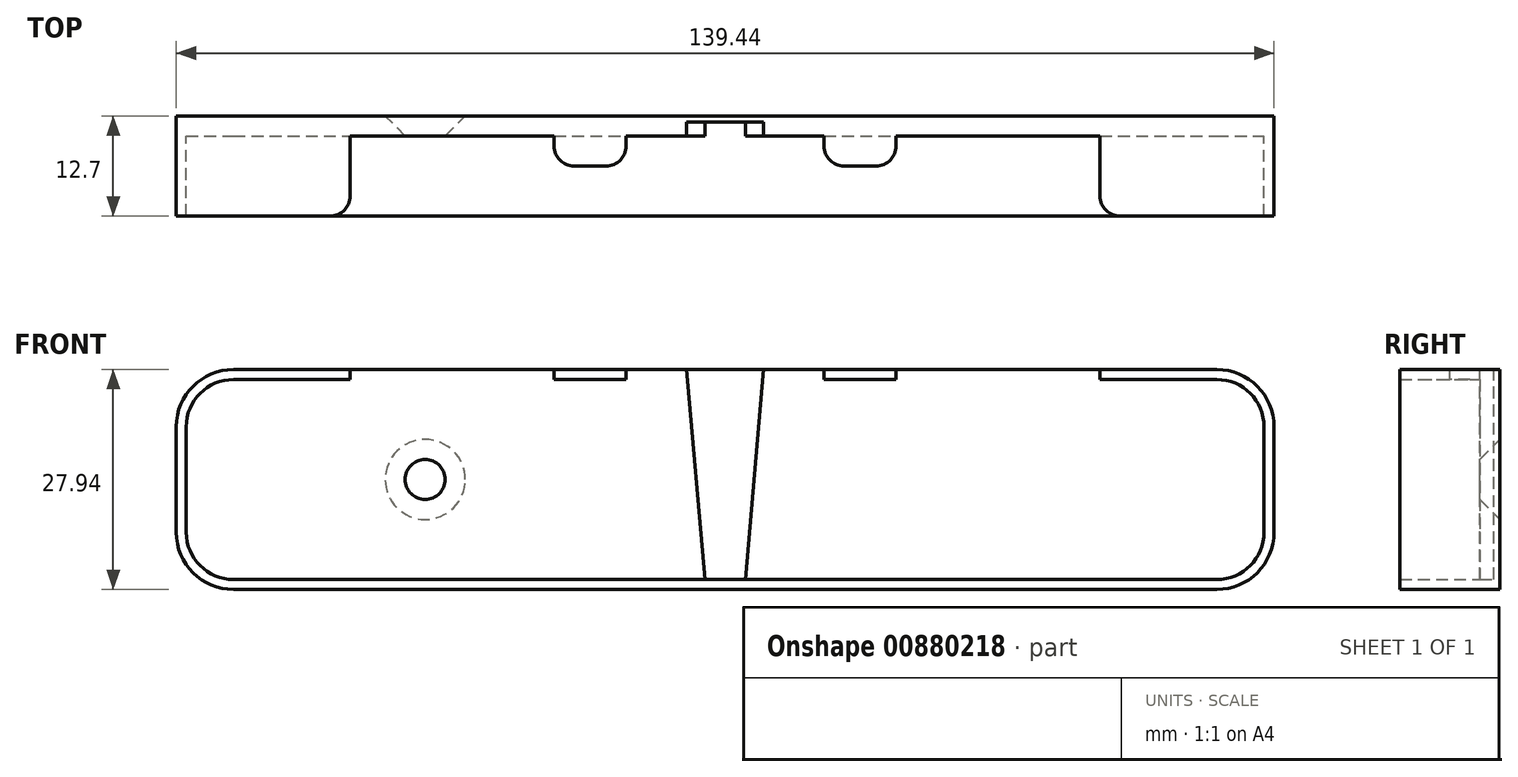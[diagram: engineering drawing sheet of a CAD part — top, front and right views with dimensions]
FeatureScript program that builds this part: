
annotation { "Feature Type Name" : "Feature", "Feature Type Description" : "" }
export const myFeature = defineFeature(function(context is Context, id is Id, definition is map)
    precondition{}
    {
        {
            var Q0;
            Q0=qCreatedBy(makeId("Front.planeOp"),FACE);
            var sketch = newSketch(context, id + "F0", { "sketchPlane" : qUnion([Q0])});
            skLineSegment(sketch, "E0.bottom", {"start": v(-69.72, 13.97) * mm, "end": v(69.72, 13.97) * mm});
            skLineSegment(sketch, "E0.top", {"start": v(-69.72, -13.97) * mm, "end": v(69.72, -13.97) * mm});
            skLineSegment(sketch, "E0.left", {"start": v(-69.72, 13.97) * mm, "end": v(-69.72, -13.97) * mm});
            skLineSegment(sketch, "E0.right", {"start": v(69.72, 13.97) * mm, "end": v(69.72, -13.97) * mm});
            skPoint(sketch, "E0.middle", {"position": v(0, 0) * mm});
            skLineSegment(sketch, "E1.bottom", {"start": v(-68.45, 12.7) * mm, "end": v(68.45, 12.7) * mm});
            skLineSegment(sketch, "E1.top", {"start": v(-68.45, -12.7) * mm, "end": v(68.45, -12.7) * mm});
            skLineSegment(sketch, "E1.left", {"start": v(-68.45, 12.7) * mm, "end": v(-68.45, -12.7) * mm});
            skLineSegment(sketch, "E1.right", {"start": v(68.45, 12.7) * mm, "end": v(68.45, -12.7) * mm});
            skLineSegment(sketch, "E2", {"start": v(47.62, 12.7) * mm, "end": v(47.62, 13.97) * mm});
            skLineSegment(sketch, "E3", {"start": v(21.72, 12.7) * mm, "end": v(21.72, 13.97) * mm});
            skLineSegment(sketch, "E4", {"start": v(12.57, 12.7) * mm, "end": v(12.57, 13.97) * mm});
            skLineSegment(sketch, "E5.MirrorCS", {"start": v(-12.57, 12.7) * mm, "end": v(-12.57, 13.97) * mm});
            skLineSegment(sketch, "E6.MirrorCS", {"start": v(-21.72, 12.7) * mm, "end": v(-21.72, 13.97) * mm});
            skLineSegment(sketch, "E7.MirrorCS", {"start": v(-47.62, 12.7) * mm, "end": v(-47.62, 13.97) * mm});
            skLineSegment(sketch, "E8", {"start": v(2.54, -12.94) * mm, "end": v(4.9, 13.97) * mm});
            skLineSegment(sketch, "E9.MirrorCS", {"start": v(-2.54, -12.94) * mm, "end": v(-4.9, 13.97) * mm});
            skSolve(sketch);
        }
        {
            var Q0;
            Q0=makeQuery(id+"F0.imprint","IMPRINT",FACE,{"disambiguationData":[TD([[makeQuery(id+"F0.imprint","IMPRINT",EDGE,{"derivedFrom":sQuery(id+"F0.wireOp",EDGE,"E0.bottom")}),-1.0]])]});
            extrude(context, id + "F1", {"entities" : qUnion([Q0]), "depth" : 12.7 * mm, "offsetDistance" : 25.4 * mm});
        }
        {
            var Q0;
            Q0=makeQuery(id+"F0.imprint","IMPRINT",FACE,{"disambiguationData":[TD([[makeQuery(id+"F0.imprint","IMPRINT",EDGE,{"derivedFrom":sQuery(id+"F0.wireOp",EDGE,"E1.bottom")}),-1.0]])]});
            extrude(context, id + "F2", {"entities" : qUnion([Q0]), "operationType" : NewBodyOperationType.ADD, "depth" : 2.54 * mm, "offsetDistance" : 25.4 * mm});
        }
        {
            var Q0;
            Q0=makeQuery(id+"F1.opExtrude","SWEPT_EDGE",EDGE,{"disambiguationData":[OSD([sQuery(id+"F0.wireOp",EDGE,"E1.bottom"),sQuery(id+"F0.wireOp",EDGE,"E1.left")])]});
            var Q1;
            Q1=makeQuery(id+"F1.opExtrude","SWEPT_EDGE",EDGE,{"disambiguationData":[OSD([sQuery(id+"F0.wireOp",EDGE,"E1.top"),sQuery(id+"F0.wireOp",EDGE,"E1.left")])]});
            var Q2;
            Q2=makeQuery(id+"F1.opExtrude","SWEPT_EDGE",EDGE,{"disambiguationData":[OSD([sQuery(id+"F0.wireOp",EDGE,"E1.bottom"),sQuery(id+"F0.wireOp",EDGE,"E1.right")])]});
            var Q3;
            Q3=makeQuery(id+"F1.opExtrude","SWEPT_EDGE",EDGE,{"disambiguationData":[OSD([sQuery(id+"F0.wireOp",EDGE,"E1.top"),sQuery(id+"F0.wireOp",EDGE,"E1.right")])]});
            fillet(context, id + "F3", {"entities" : qUnion([Q0, Q1, Q2, Q3]), "radius" : 6 * mm, "tangentPropagation" : true, "allowEdgeOverflow" : false});
        }
        {
            var Q0;
            Q0=makeQuery(id+"F1.opExtrude","SWEPT_EDGE",EDGE,{"disambiguationData":[OSD([sQuery(id+"F0.wireOp",EDGE,"E0.bottom"),sQuery(id+"F0.wireOp",EDGE,"E0.left")])]});
            var Q1;
            Q1=makeQuery(id+"F1.opExtrude","SWEPT_EDGE",EDGE,{"disambiguationData":[OSD([sQuery(id+"F0.wireOp",EDGE,"E0.top"),sQuery(id+"F0.wireOp",EDGE,"E0.left")])]});
            var Q2;
            Q2=makeQuery(id+"F1.opExtrude","SWEPT_EDGE",EDGE,{"disambiguationData":[OSD([sQuery(id+"F0.wireOp",EDGE,"E0.top"),sQuery(id+"F0.wireOp",EDGE,"E0.right")])]});
            var Q3;
            Q3=makeQuery(id+"F1.opExtrude","SWEPT_EDGE",EDGE,{"disambiguationData":[OSD([sQuery(id+"F0.wireOp",EDGE,"E0.bottom"),sQuery(id+"F0.wireOp",EDGE,"E0.right")])]});
            fillet(context, id + "F4", {"entities" : qUnion([Q0, Q1, Q2, Q3]), "radius" : 7.26 * mm, "tangentPropagation" : true, "allowEdgeOverflow" : false});
        }
        {
            var Q0;
            Q0=makeQuery(id+"F2.opExtrude","CAP_FACE",FACE,{"disambiguationData":[OSD([sQuery(id+"F0.wireOp",EDGE,"E1.bottom"),sQuery(id+"F0.wireOp",EDGE,"E1.top"),sQuery(id+"F0.wireOp",EDGE,"E1.left"),sQuery(id+"F0.wireOp",EDGE,"E1.right")])],"isStart":false});
            var sketch = newSketch(context, id + "F5", { "sketchPlane" : qUnion([Q0])});
            skCircle(sketch, "E10", {"center": v(-38.1, 0) * mm, "radius": 2.54 * mm});
            skCircle(sketch, "E11.MirrorC", {"center": v(38.1, 0) * mm, "radius": 2.54 * mm});
            skSolve(sketch);
        }
        {
            var Q0;
            Q0=makeQuery(id+"F5.imprint","IMPRINT",FACE,{"disambiguationData":[TD([[makeQuery(id+"F5.imprint","IMPRINT",EDGE,{"derivedFrom":sQuery(id+"F5.wireOp",EDGE,"E10")}),1.0]])]});
            var Q1;
            Q1=makeQuery(id+"F5.imprint","IMPRINT",FACE,{"disambiguationData":[TD([[makeQuery(id+"F5.imprint","IMPRINT",EDGE,{"derivedFrom":sQuery(id+"F5.wireOp",EDGE,"E11.MirrorC")}),-1.0]])]});
            extrude(context, id + "F6", {"entities" : qUnion([Q0, Q1]), "operationType" : NewBodyOperationType.REMOVE, "oppositeDirection" : true, "depth" : 25.4 * mm, "offsetDistance" : 25.4 * mm, "hasDraft" : true, "draftAngle" : 45 * degree});
        }
        {
            var Q0;
            {var subQ0=sQuery(id+"F0.wireOp",EDGE,"E3");Q0=makeQuery(id+"F0.imprint","IMPRINT",FACE,{"disambiguationData":[TD([[makeQuery(id+"F0.imprint","IMPRINT",EDGE,{"derivedFrom":subQ0}),1.0]])]});}
            var Q1;
            {var subQ0=sQuery(id+"F0.wireOp",EDGE,"E5.MirrorCS");Q1=makeQuery(id+"F0.imprint","IMPRINT",FACE,{"disambiguationData":[TD([[makeQuery(id+"F0.imprint","IMPRINT",EDGE,{"derivedFrom":subQ0}),1.0]])]});}
            extrude(context, id + "F7", {"entities" : qUnion([Q0, Q1]), "operationType" : NewBodyOperationType.ADD, "depth" : 6.35 * mm, "offsetDistance" : 25.4 * mm});
        }
        {
            var Q0;
            {var subQ0=sQuery(id+"F0.wireOp",EDGE,"E2");Q0=makeQuery(id+"F0.imprint","IMPRINT",FACE,{"disambiguationData":[TD([[makeQuery(id+"F0.imprint","IMPRINT",EDGE,{"derivedFrom":subQ0}),1.0]])]});}
            var Q1;
            {var subQ0=sQuery(id+"F0.wireOp",EDGE,"E4");Q1=makeQuery(id+"F0.imprint","IMPRINT",FACE,{"disambiguationData":[TD([[makeQuery(id+"F0.imprint","IMPRINT",EDGE,{"derivedFrom":subQ0}),1.0]])]});}
            var Q2;
            {var subQ0=sQuery(id+"F0.wireOp",EDGE,"E6.MirrorCS");Q2=makeQuery(id+"F0.imprint","IMPRINT",FACE,{"disambiguationData":[TD([[makeQuery(id+"F0.imprint","IMPRINT",EDGE,{"derivedFrom":subQ0}),1.0]])]});}
            var Q3;
            {var subQ0=sQuery(id+"F0.wireOp",EDGE,"E5.MirrorCS");Q3=makeQuery(id+"F0.imprint","IMPRINT",FACE,{"disambiguationData":[TD([[makeQuery(id+"F0.imprint","IMPRINT",EDGE,{"derivedFrom":subQ0}),-1.0]])]});}
            extrude(context, id + "F8", {"entities" : qUnion([Q0, Q1, Q2, Q3]), "operationType" : NewBodyOperationType.ADD, "depth" : 2.54 * mm, "offsetDistance" : 25.4 * mm});
        }
        {
            var Q0;
            Q0=makeQuery(id+"F1.opExtrude","CAP_EDGE",EDGE,{"disambiguationData":[OSD([sQuery(id+"F0.wireOp",EDGE,"E2")])],"isStart":false});
            var Q1;
            Q1=makeQuery(id+"F7.opExtrude","CAP_EDGE",EDGE,{"disambiguationData":[OSD([sQuery(id+"F0.wireOp",EDGE,"E3")])],"isStart":false});
            var Q2;
            Q2=makeQuery(id+"F7.opExtrude","CAP_EDGE",EDGE,{"disambiguationData":[OSD([sQuery(id+"F0.wireOp",EDGE,"E4")])],"isStart":false});
            var Q3;
            Q3=makeQuery(id+"F7.opExtrude","CAP_EDGE",EDGE,{"disambiguationData":[OSD([sQuery(id+"F0.wireOp",EDGE,"E5.MirrorCS")])],"isStart":false});
            var Q4;
            Q4=makeQuery(id+"F7.opExtrude","CAP_EDGE",EDGE,{"disambiguationData":[OSD([sQuery(id+"F0.wireOp",EDGE,"E6.MirrorCS")])],"isStart":false});
            var Q5;
            Q5=makeQuery(id+"F1.opExtrude","CAP_EDGE",EDGE,{"disambiguationData":[OSD([sQuery(id+"F0.wireOp",EDGE,"E7.MirrorCS")])],"isStart":false});
            fillet(context, id + "F9", {"entities" : qUnion([Q0, Q1, Q2, Q3, Q4, Q5]), "radius" : 2.54 * mm, "tangentPropagation" : true, "allowEdgeOverflow" : false});
        }
        {
            var Q0;
            {var subQ0=sQuery(id+"F0.wireOp",EDGE,"E9.MirrorCS");var subQ1=sQuery(id+"F0.wireOp",EDGE,"E1.bottom");var subQ2=makeQuery(id+"F0.imprint","INTERSECT",VERTEX,{"derivedFrom":[subQ1,subQ0]});Q0=makeQuery(id+"F0.imprint","IMPRINT",FACE,{"disambiguationData":[TD([[makeQuery(id+"F0.imprint","IMPRINT",EDGE,{"disambiguationData":[TD([[subQ2,-1.0]])],"derivedFrom":subQ1}),-1.0]])]});}
            var Q1;
            {var subQ0=sQuery(id+"F0.wireOp",EDGE,"E8");var subQ1=sQuery(id+"F0.wireOp",EDGE,"E0.bottom");var subQ2=makeQuery(id+"F0.imprint","INTERSECT",VERTEX,{"derivedFrom":[subQ1,subQ0]});Q1=makeQuery(id+"F0.imprint","IMPRINT",FACE,{"disambiguationData":[TD([[makeQuery(id+"F0.imprint","IMPRINT",EDGE,{"disambiguationData":[TD([[subQ2,1.0]])],"derivedFrom":subQ1}),-1.0]])]});}
            extrude(context, id + "F10", {"entities" : qUnion([Q0, Q1]), "operationType" : NewBodyOperationType.ADD, "depth" : 0.76 * mm, "offsetDistance" : 25.4 * mm});
        }
    });
